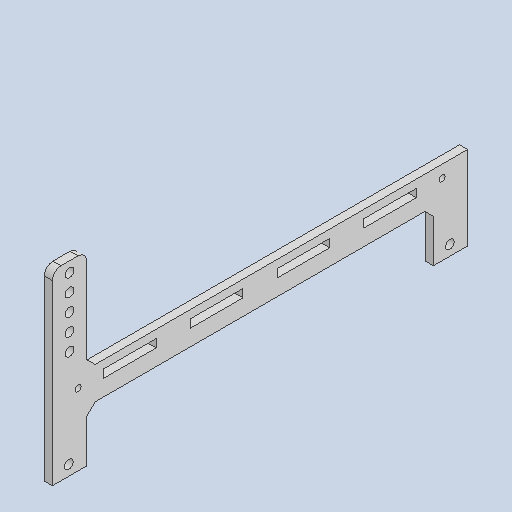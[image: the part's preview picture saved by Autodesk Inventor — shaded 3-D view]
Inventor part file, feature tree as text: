
AUTODESK INVENTOR PART (.ipt)
format: ipt  version: 2022.1 (Build 261234020, 234B)  size: 194,560 bytes
history: native  units: mm
features: other x6, sketch x5, hole x3, extrude x2, chamfer x2, reference x2, fillet x1
ambient origin geometry x8: Origin, YZ Plane, XZ Plane, XY Plane, X Axis, Y Axis, Z Axis, Center Point
bodies: Solid1 (feature_tree)
feature tree (21):
  extrude  "Extrusion1"  Depth=38.1mm
  sketch  "Sketch2"  dims[d4=38.1mm d5=24.0mm]
  extrude  "Extrusion3"  Depth=24.0mm
  chamfer  "Chamfer1"  Distance=39.0017mm
  chamfer  "Chamfer2"  Distance=6.0mm
  fillet  "Fillet1"  Radius=39.0017mm
  sketch  "Sketch4"  dims[d16=308.4068mm]
  sketch  "Sketch5"  dims[d17=6.0mm d18=39.0017mm d21=6.0mm d22=39.0017mm d23=25.4mm d24=6.0mm d25=39.0017mm d26=25.4mm d27=6.0mm d28=39.0017mm d29=25.4mm d33=6.0mm d34=0.0mm d37=12.7mm d38=0.0mm d39=0.0mm d40=6.35mm d41=3.175mm d42=45.0deg d43=6.35mm d44=3.175mm d45=45.0deg d46=6.35mm d49=25.4mm d50=6.35mm d51=7.62mm d52=50.0mm d54=12.7mm d55=10.0mm d57=25.4mm d61=38.1mm d62=50.099999mm d63=3.2512mm d64=3.2512mm d65=19.05mm d66=19.05mm d69=6.604mm d70=19.05mm d71=14.5542mm d72=4.3688mm d73=90.0deg d74=17.0942mm d75=20.594885mm d76=6.604mm d77=19.05mm d78=14.5542mm d79=4.3688mm d80=90.0deg d81=17.0942mm d82=20.594885mm d83=4.4958mm d84=19.05mm d85=8.001mm d86=3.9878mm d87=90.0deg d88=17.0942mm d89=20.594885mm d90=38.1mm]
  hole  "Hole1"  [1 undecoded]
  hole  "Hole2"  [1 undecoded]
  hole  "Hole3"  [1 undecoded]
  sketch  "Sketch1"  dims[d1=38.1mm d2=38.1mm]
  reference  "Reference1"
  reference  "Reference2"
  sketch  "Sketch3"  dims[d6=76.2mm]
  other  "<userpath>\Desktop\P3 Bracket Files\V3 Baseplate.iam"
  other  "V3 Baseplate.iam"
  other  "QBot:1"
  other  "A002-596_A002-596-01_32"
  other  "C005-958_01_74"
  other  "C005-958_01_101"
note: 3 required parameter values undecoded (feature->parameter linkage not recoverable at this tier; creation-order binding heuristic only, values carry confidence <= 0.55)
